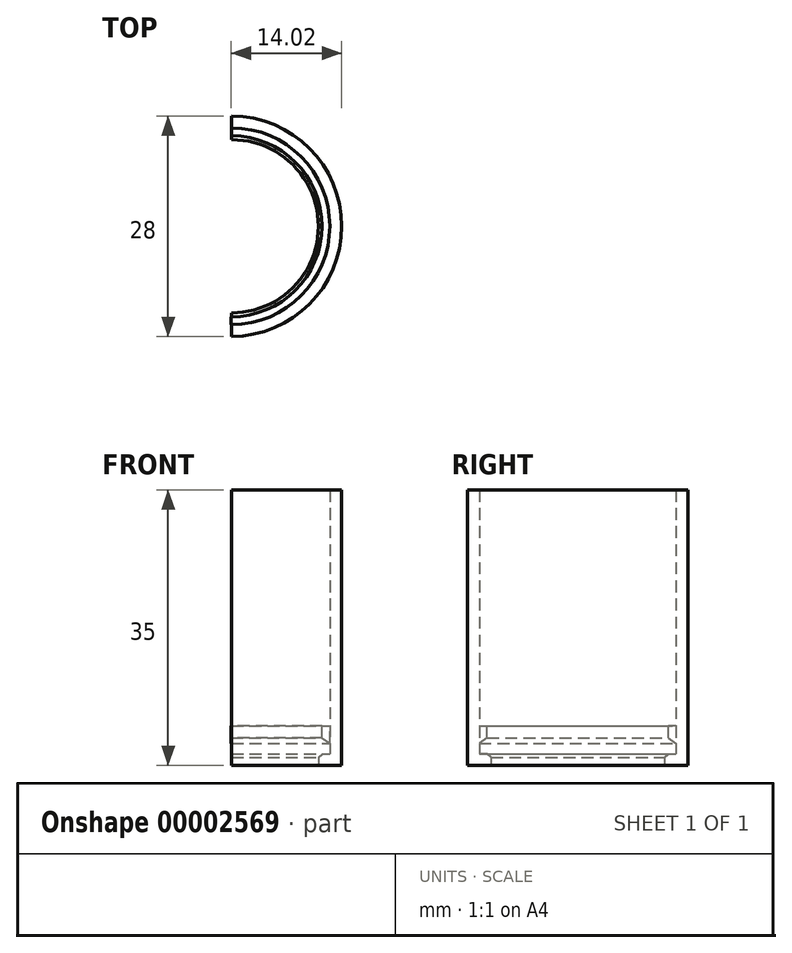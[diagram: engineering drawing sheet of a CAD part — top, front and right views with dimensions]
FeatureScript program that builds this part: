
annotation { "Feature Type Name" : "Feature", "Feature Type Description" : "" }
export const myFeature = defineFeature(function(context is Context, id is Id, definition is map)
    precondition{}
    {
        {
            var Q0;
            Q0=qCreatedBy(makeId("Top.planeOp"),FACE);
            var sketch = newSketch(context, id + "F0", { "sketchPlane" : qUnion([Q0])});
            skLineSegment(sketch, "E0", {"start": v(0, 11) * mm, "end": v(0, 12.5) * mm});
            skLineSegment(sketch, "E1", {"start": v(0, 12.5) * mm, "end": v(0, 14) * mm});
            skLineSegment(sketch, "E2.0.MirrorCS", {"start": v(0, -11) * mm, "end": v(0, -12.5) * mm});
            skLineSegment(sketch, "E3.0.MirrorCS", {"start": v(0, -12.5) * mm, "end": v(0, -14) * mm});
            skArc(sketch, "E4", {"start": v(0, -12.5) * mm, "mid": v(12.47, 0) * mm, "end": v(0, 12.5) * mm});
            skArc(sketch, "E5", {"start": v(0, -14) * mm, "mid": v(13.97, 0) * mm, "end": v(0, 14) * mm});
            skArc(sketch, "E6", {"start": v(0, -11) * mm, "mid": v(11.03, 0) * mm, "end": v(0, 11) * mm});
            skSolve(sketch);
        }
        {
            var Q0;
            Q0=makeQuery(id+"F0.imprint","IMPRINT",FACE,{"disambiguationData":[TD([[makeQuery(id+"F0.imprint","IMPRINT",EDGE,{"derivedFrom":sQuery(id+"F0.wireOp",EDGE,"E1")}),-1.0]])]});
            extrude(context, id + "F1", {"entities" : qUnion([Q0]), "depth" : 35 * mm});
        }
        {
            var Q0;
            Q0 = qSketchRegion(id + "F0", true);
            extrude(context, id + "F2", {"entities" : qUnion([Q0]), "operationType" : NewBodyOperationType.ADD, "depth" : 1.5 * mm});
        }
        {
            var Q0;
            {var subQ0=sQuery(id+"F0.wireOp",EDGE,"E1");Q0=makeQuery(id+"F2.boolean.opBoolean","MERGE",FACE,{"derivedFrom":[makeQuery(id+"F1.opExtrude","SWEPT_FACE",FACE,{"disambiguationData":[OSD([subQ0])]}),makeQuery(id+"F2.opExtrude","SWEPT_FACE",FACE,{"disambiguationData":[OSD([sQuery(id+"F0.wireOp",EDGE,"E0"),subQ0])]})]});}
            var sketch = newSketch(context, id + "F3", { "sketchPlane" : qUnion([Q0])});
            skLineSegment(sketch, "E7.bottom", {"start": v(-12.5, 3.5) * mm, "end": v(-11.5, 3.5) * mm});
            skLineSegment(sketch, "E7.top", {"start": v(-12.5, 5) * mm, "end": v(-11.5, 5) * mm});
            skLineSegment(sketch, "E7.left", {"start": v(-12.5, 3.5) * mm, "end": v(-12.5, 5) * mm});
            skLineSegment(sketch, "E7.right", {"start": v(-11.5, 3.5) * mm, "end": v(-11.5, 5) * mm});
            skLineSegment(sketch, "E8", {"start": v(-11.5, 3.5) * mm, "end": v(-12.5, 2.8) * mm});
            skLineSegment(sketch, "E9", {"start": v(-12.5, 2.8) * mm, "end": v(-12.5, 3.5) * mm});
            skSolve(sketch);
        }
        {
            var Q0;
            Q0=makeQuery(id+"F3.imprint","IMPRINT",FACE,{"disambiguationData":[TD([[makeQuery(id+"F3.imprint","IMPRINT",EDGE,{"derivedFrom":sQuery(id+"F3.wireOp",EDGE,"E7.bottom")}),1.0]])]});
            var Q1;
            Q1=makeQuery(id+"F3.imprint","IMPRINT",FACE,{"disambiguationData":[TD([[makeQuery(id+"F3.imprint","IMPRINT",EDGE,{"derivedFrom":sQuery(id+"F3.wireOp",EDGE,"E7.bottom")}),-1.0]])]});
            var Q2;
            Q2=makeQuery(id+"F2.boolean.opBoolean","INTERSECT",EDGE,{"derivedFrom":[makeQuery(id+"F1.opExtrude","SWEPT_FACE",FACE,{"disambiguationData":[OSD([sQuery(id+"F0.wireOp",EDGE,"E4")])]}),makeQuery(id+"F2.opExtrude","CAP_FACE",FACE,{"disambiguationData":[OSD([sQuery(id+"F0.wireOp",EDGE,"E0"),sQuery(id+"F0.wireOp",EDGE,"E1"),sQuery(id+"F0.wireOp",EDGE,"E2.0.MirrorCS"),sQuery(id+"F0.wireOp",EDGE,"E3.0.MirrorCS"),sQuery(id+"F0.wireOp",EDGE,"E5"),sQuery(id+"F0.wireOp",EDGE,"E6")])],"isStart":false})]});
            revolve(context, id + "F4", {"entities" : qUnion([Q0, Q1]), "axis" : qUnion([Q2]), "revolveType" : RevolveType.ONE_DIRECTION, "oppositeDirection" : true, "angle" : 180 * degree});
        }
        {
            var Q0;
            Q0=makeQuery(id+"F2.opExtrude","CAP_EDGE",EDGE,{"disambiguationData":[OSD([sQuery(id+"F0.wireOp",EDGE,"E6")])],"isStart":false});
            chamfer(context, id + "F5", {"entities" : qUnion([Q0]), "width" : .5 * mm, "tangentPropagation" : true});
        }
    });
